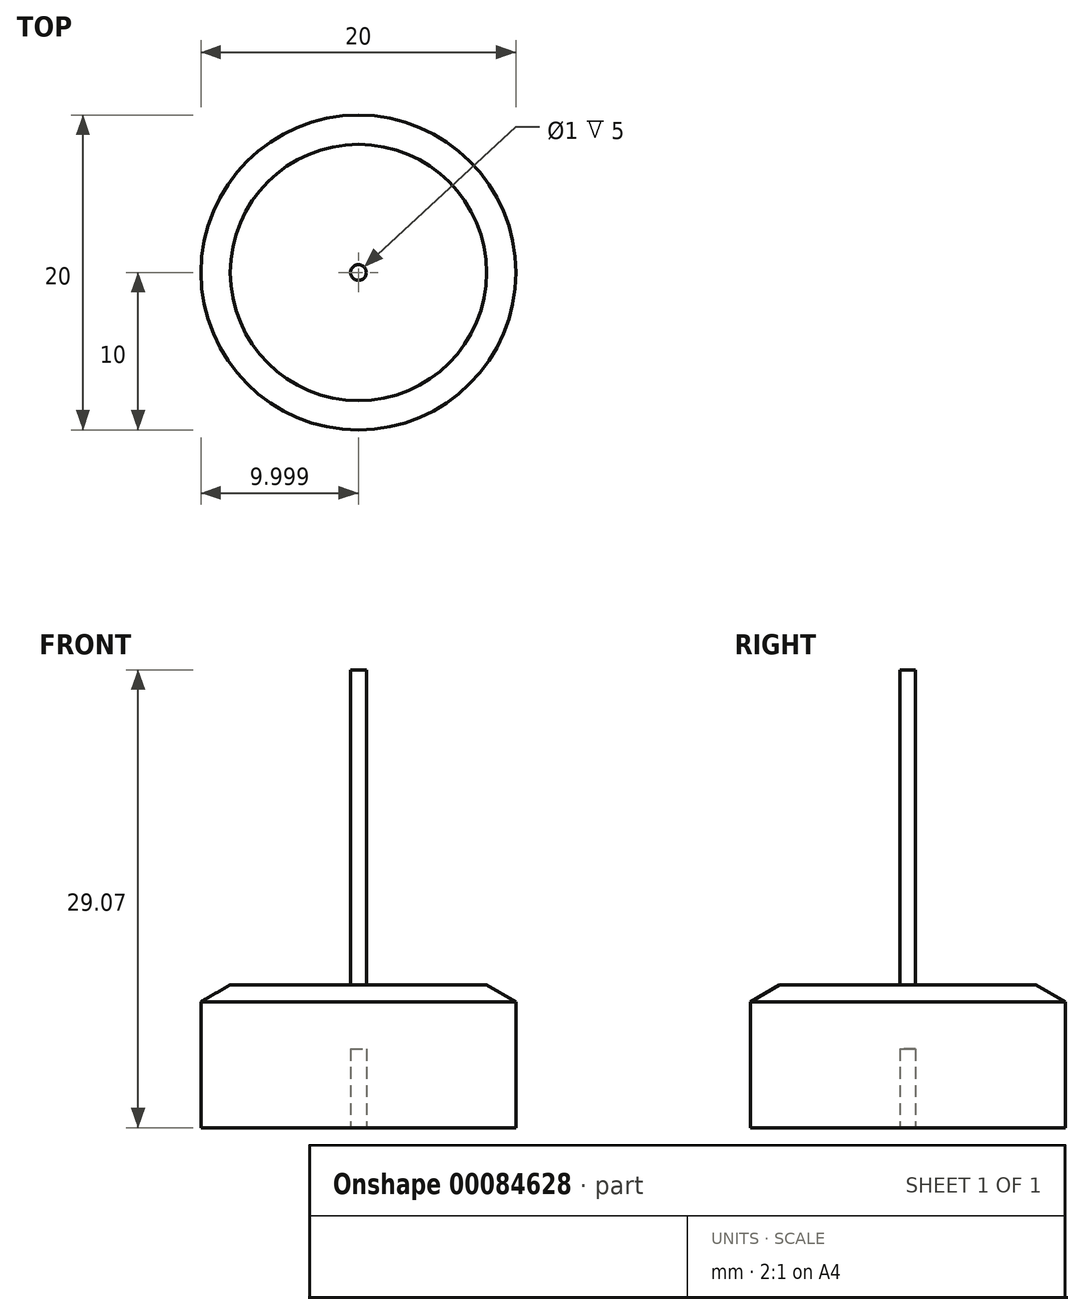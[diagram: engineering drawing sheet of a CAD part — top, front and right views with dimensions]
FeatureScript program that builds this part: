
annotation { "Feature Type Name" : "Feature", "Feature Type Description" : "" }
export const myFeature = defineFeature(function(context is Context, id is Id, definition is map)
    precondition{}
    {
        {
            var Q0;
            Q0=qCreatedBy(makeId("Front.planeOp"),FACE);
            var sketch = newSketch(context, id + "F0", { "sketchPlane" : qUnion([Q0])});
            skLineSegment(sketch, "E0.bottom", {"start": v(-30.55, 8) * mm, "end": v(-20.55, 8) * mm});
            skLineSegment(sketch, "E0.top", {"start": v(-30.55, 0) * mm, "end": v(-21.05, 0) * mm});
            skLineSegment(sketch, "E0.left", {"start": v(-30.55, 8) * mm, "end": v(-30.55, 0) * mm});
            skPoint(sketch, "E1", {"position": v(-20.55, 8) * mm});
            skPoint(sketch, "E2", {"position": v(-20.55, 0) * mm});
            skPoint(sketch, "E3", {"position": v(-20.55, 9.07) * mm});
            skLineSegment(sketch, "E4", {"start": v(-20.55, 8) * mm, "end": v(-20.55, 9.07) * mm});
            skLineSegment(sketch, "E5", {"start": v(-30.55, 8) * mm, "end": v(-28.7, 9.07) * mm});
            skLineSegment(sketch, "E6", {"start": v(-28.7, 9.07) * mm, "end": v(-20.55, 9.07) * mm});
            skLineSegment(sketch, "E7", {"start": v(-20.55, 8) * mm, "end": v(-20.55, 5) * mm});
            skPoint(sketch, "E0.right.end.orphan", {"position": v(-10.55, 0) * mm});
            skPoint(sketch, "E8.start.orphan", {"position": v(-10.55, 8) * mm});
            skLineSegment(sketch, "E9", {"start": v(-20.55, 9.07) * mm, "end": v(-20.55, 29.07) * mm});
            skLineSegment(sketch, "E10", {"start": v(-20.55, 29.07) * mm, "end": v(-21.05, 29.07) * mm});
            skLineSegment(sketch, "E11", {"start": v(-21.05, 29.07) * mm, "end": v(-21.05, 0) * mm});
            skPoint(sketch, "E12.start.orphan", {"position": v(-20.55, 4) * mm});
            skLineSegment(sketch, "E13", {"start": v(-20.55, 5) * mm, "end": v(-21.05, 5) * mm});
            skPoint(sketch, "E14", {"position": v(-20.55, 5) * mm});
            skSolve(sketch);
        }
        {
            var Q0;
            {var subQ0=sQuery(id+"F0.wireOp",EDGE,"E9");Q0=makeQuery(id+"F0.imprint","IMPRINT",FACE,{"disambiguationData":[TD([[makeQuery(id+"F0.imprint","IMPRINT",EDGE,{"derivedFrom":subQ0}),1.0]])]});}
            var Q1;
            {var subQ5=sQuery(id+"F0.wireOp",EDGE,"E0.top");Q1=makeQuery(id+"F0.imprint","IMPRINT",FACE,{"disambiguationData":[TD([[makeQuery(id+"F0.imprint","IMPRINT",EDGE,{"derivedFrom":subQ5}),1.0]])]});}
            var Q2;
            {var subQ0=sQuery(id+"F0.wireOp",EDGE,"E5");Q2=makeQuery(id+"F0.imprint","IMPRINT",FACE,{"disambiguationData":[TD([[makeQuery(id+"F0.imprint","IMPRINT",EDGE,{"derivedFrom":subQ0}),-1.0]])]});}
            var Q3;
            {var subQ0=sQuery(id+"F0.wireOp",EDGE,"E7");Q3=makeQuery(id+"F0.imprint","IMPRINT",FACE,{"disambiguationData":[TD([[makeQuery(id+"F0.imprint","IMPRINT",EDGE,{"derivedFrom":subQ0}),-1.0]])]});}
            var Q4;
            {var subQ0=sQuery(id+"F0.wireOp",EDGE,"E4");Q4=makeQuery(id+"F0.imprint","IMPRINT",FACE,{"disambiguationData":[TD([[makeQuery(id+"F0.imprint","IMPRINT",EDGE,{"derivedFrom":subQ0}),1.0]])]});}
            var Q5;
            Q5=sQuery(id+"F0.wireOp",EDGE,"E9");
            revolve(context, id + "F1", {"entities" : qUnion([Q0, Q1, Q2, Q3, Q4]), "axis" : qUnion([Q5]), "revolveType" : RevolveType.FULL});
        }
    });
